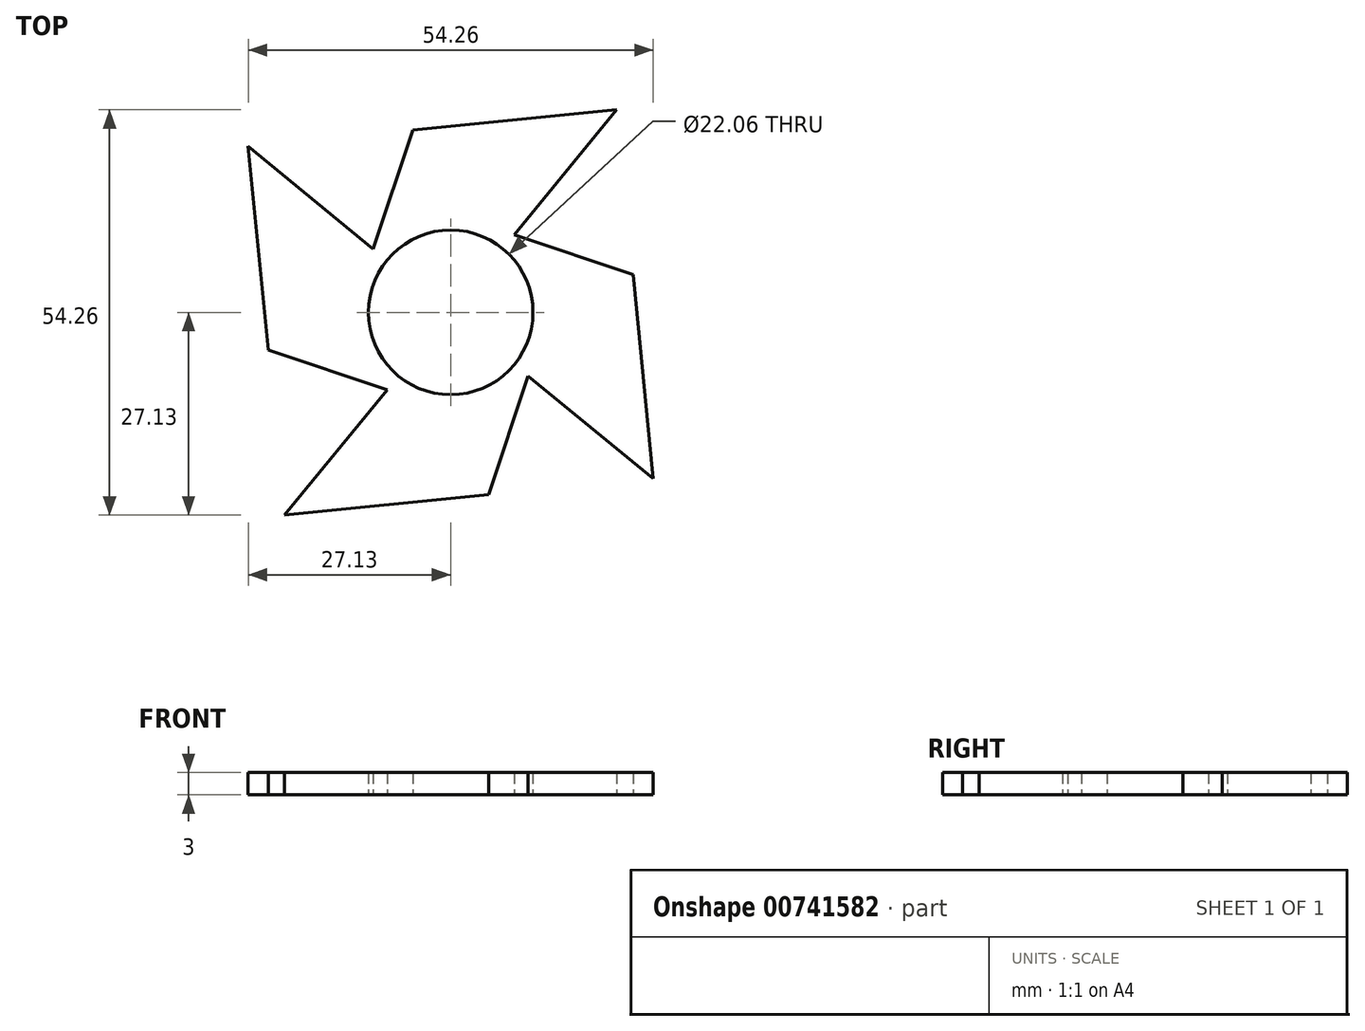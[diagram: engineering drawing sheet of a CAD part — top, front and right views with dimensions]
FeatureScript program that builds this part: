
annotation { "Feature Type Name" : "Feature", "Feature Type Description" : "" }
export const myFeature = defineFeature(function(context is Context, id is Id, definition is map)
    precondition{}
    {
        {
            var Q0;
            Q0=qCreatedBy(makeId("Top.planeOp"),FACE);
            var sketch = newSketch(context, id + "F0", { "sketchPlane" : qUnion([Q0])});
            skCircle(sketch, "E0", {"center": v(0, 0) * mm, "radius": 11.03 * mm});
            skLineSegment(sketch, "E1.trimOffspring", {"start": v(-10.38, 8.5) * mm, "end": v(-27.13, 22.26) * mm});
            skLineSegment(sketch, "E2.trimOffspring", {"start": v(-8.5, -10.38) * mm, "end": v(-22.26, -27.13) * mm});
            skLineSegment(sketch, "E3.trimOffspring", {"start": v(10.38, -8.5) * mm, "end": v(27.13, -22.26) * mm});
            skLineSegment(sketch, "E4.trimOffspring", {"start": v(8.5, 10.38) * mm, "end": v(22.26, 27.13) * mm});
            skLineSegment(sketch, "E5", {"start": v(-5.07, 24.44) * mm, "end": v(22.26, 27.13) * mm});
            skLineSegment(sketch, "E6", {"start": v(24.44, 5.07) * mm, "end": v(27.13, -22.26) * mm});
            skLineSegment(sketch, "E7", {"start": v(5.07, -24.44) * mm, "end": v(-22.26, -27.13) * mm});
            skLineSegment(sketch, "E8", {"start": v(-27.13, 22.26) * mm, "end": v(-24.44, -5.07) * mm});
            skLineSegment(sketch, "E9", {"start": v(10.38, -8.5) * mm, "end": v(5.07, -24.44) * mm});
            skLineSegment(sketch, "E10", {"start": v(8.5, 10.38) * mm, "end": v(24.44, 5.07) * mm});
            skLineSegment(sketch, "E11.trimOffspring", {"start": v(-10.38, 8.5) * mm, "end": v(-5.07, 24.44) * mm});
            skLineSegment(sketch, "E12.trimOffspring", {"start": v(-8.5, -10.38) * mm, "end": v(-24.44, -5.07) * mm});
            skSolve(sketch);
        }
        {
            var Q0;
            Q0 = qSketchRegion(id + "F0", true);
            extrude(context, id + "F1", {"entities" : qUnion([Q0]), "depth" : 3 * mm, "offsetDistance" : 25 * mm});
        }
    });
